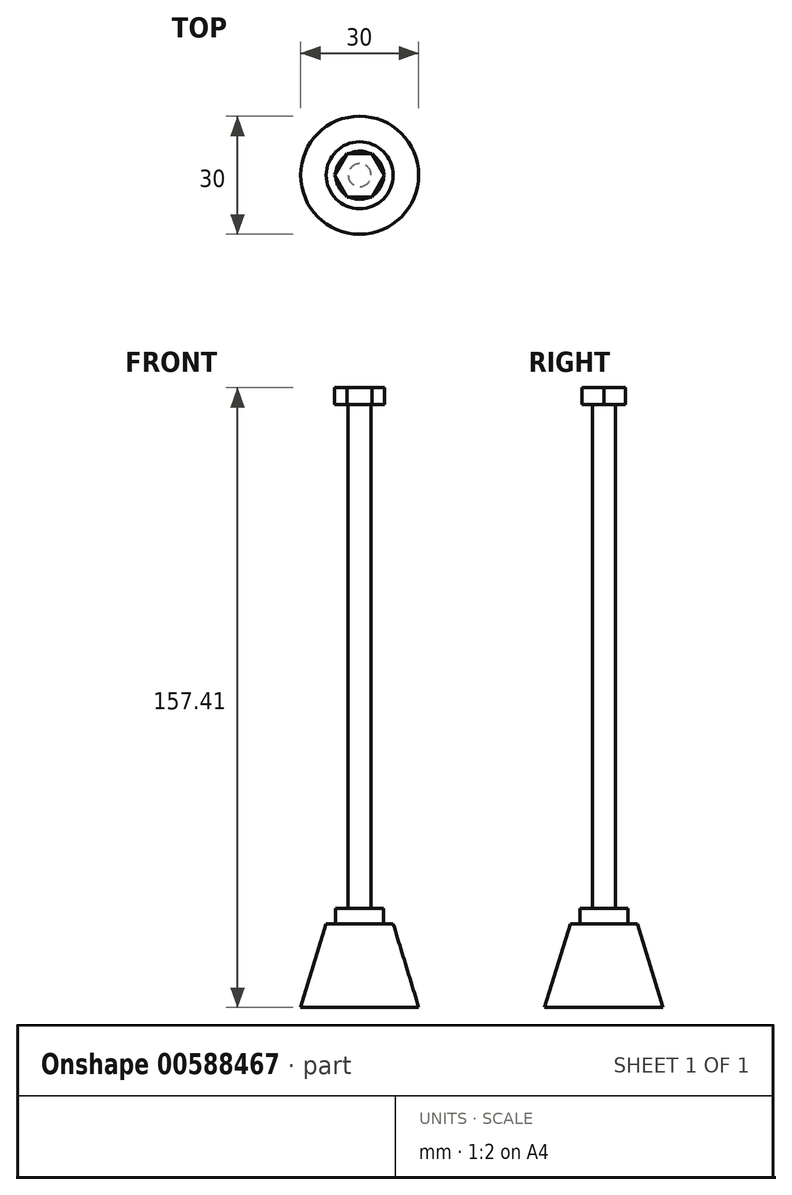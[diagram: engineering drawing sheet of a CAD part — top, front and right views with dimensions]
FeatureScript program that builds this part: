
annotation { "Feature Type Name" : "Feature", "Feature Type Description" : "" }
export const myFeature = defineFeature(function(context is Context, id is Id, definition is map)
    precondition{}
    {
        {
            var Q0;
            Q0=qCreatedBy(makeId("Front.planeOp"),FACE);
            var sketch = newSketch(context, id + "F0", { "sketchPlane" : qUnion([Q0])});
            skLineSegment(sketch, "E0", {"start": v(0, 0) * mm, "end": v(15, 0) * mm});
            skLineSegment(sketch, "E1", {"start": v(15, 0) * mm, "end": v(8.5, 21.23) * mm});
            skLineSegment(sketch, "E2", {"start": v(8.5, 21.23) * mm, "end": v(0, 21.23) * mm});
            skLineSegment(sketch, "E3", {"start": v(0, 21.23) * mm, "end": v(0, 0) * mm});
            skLineSegment(sketch, "E4", {"start": v(2.92, 21.23) * mm, "end": v(2.92, 153.1) * mm});
            skLineSegment(sketch, "E5", {"start": v(2.92, 153.1) * mm, "end": v(0, 153.1) * mm});
            skLineSegment(sketch, "E6", {"start": v(0, 153.1) * mm, "end": v(0, 21.23) * mm});
            skLineSegment(sketch, "E7", {"start": v(0, 25.08) * mm, "end": v(6.1, 25.08) * mm});
            skLineSegment(sketch, "E8", {"start": v(6.1, 25.08) * mm, "end": v(6.1, 21.23) * mm});
            skSolve(sketch);
        }
        {
            var Q0;
            Q0 = qSketchRegion(id + "F0", true);
            var Q1;
            Q1=sQuery(id+"F0.wireOp",EDGE,"E6");
            revolve(context, id + "F1", {"entities" : qUnion([Q0]), "axis" : qUnion([Q1]), "revolveType" : RevolveType.FULL});
        }
        {
            var Q0;
            Q0=makeQuery(id+"F1.opRevolve","SWEPT_FACE",FACE,{"disambiguationData":[OSD([sQuery(id+"F0.wireOp",EDGE,"E5")])]});
            var sketch = newSketch(context, id + "F2", { "sketchPlane" : qUnion([Q0])});
            skCircle(sketch, "E9.cCircle", {"center": v(0, 0) * mm, "radius": 5.5 * mm, "construction": true});
            skLineSegment(sketch, "E9.0", {"start": v(3.16, 5.5) * mm, "end": v(6.35, 0.01) * mm});
            skLineSegment(sketch, "E9.1", {"start": v(6.35, 0.01) * mm, "end": v(3.19, -5.5) * mm});
            skLineSegment(sketch, "E9.2", {"start": v(3.19, -5.5) * mm, "end": v(-3.16, -5.5) * mm});
            skLineSegment(sketch, "E9.3", {"start": v(-3.16, -5.5) * mm, "end": v(-6.35, -0.01) * mm});
            skLineSegment(sketch, "E9.4", {"start": v(-6.35, -0.01) * mm, "end": v(-3.19, 5.5) * mm});
            skLineSegment(sketch, "E9.5", {"start": v(-3.19, 5.5) * mm, "end": v(3.16, 5.5) * mm});
            skPoint(sketch, "E9.0.midPoint", {"position": v(4.76, 2.76) * mm});
            skSolve(sketch);
        }
        {
            var Q0;
            Q0 = qSketchRegion(id + "F2", true);
            extrude(context, id + "F3", {"entities" : qUnion([Q0]), "operationType" : NewBodyOperationType.ADD, "depth" : 4.3 * mm, "offsetDistance" : 25 * mm});
        }
    });
